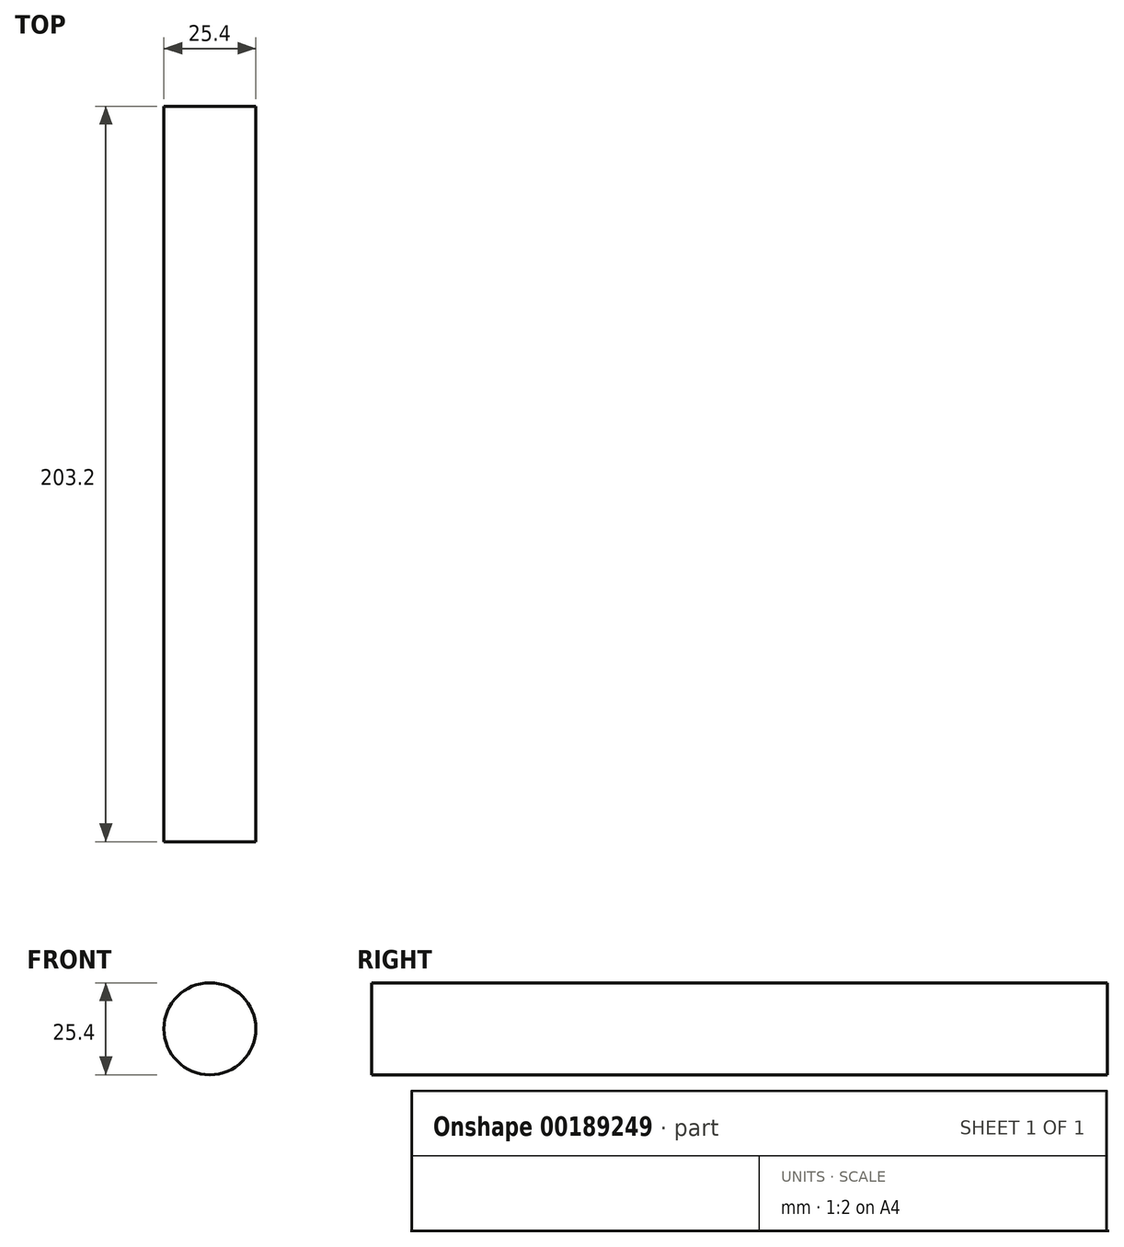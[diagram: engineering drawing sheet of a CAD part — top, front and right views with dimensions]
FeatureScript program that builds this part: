
annotation { "Feature Type Name" : "Feature", "Feature Type Description" : "" }
export const myFeature = defineFeature(function(context is Context, id is Id, definition is map)
    precondition{}
    {
        {
            var Q0;
            Q0=qCreatedBy(makeId("Front.planeOp"),FACE);
            var sketch = newSketch(context, id + "F0", { "sketchPlane" : qUnion([Q0])});
            skCircle(sketch, "E0", {"center": v(0, 0) * mm, "radius": 12.7 * mm});
            skSolve(sketch);
        }
        {
            var Q0;
            Q0 = qSketchRegion(id + "F0", true);
            extrude(context, id + "F1", {"entities" : qUnion([Q0]), "depth" : 203.2 * mm});
        }
    });
